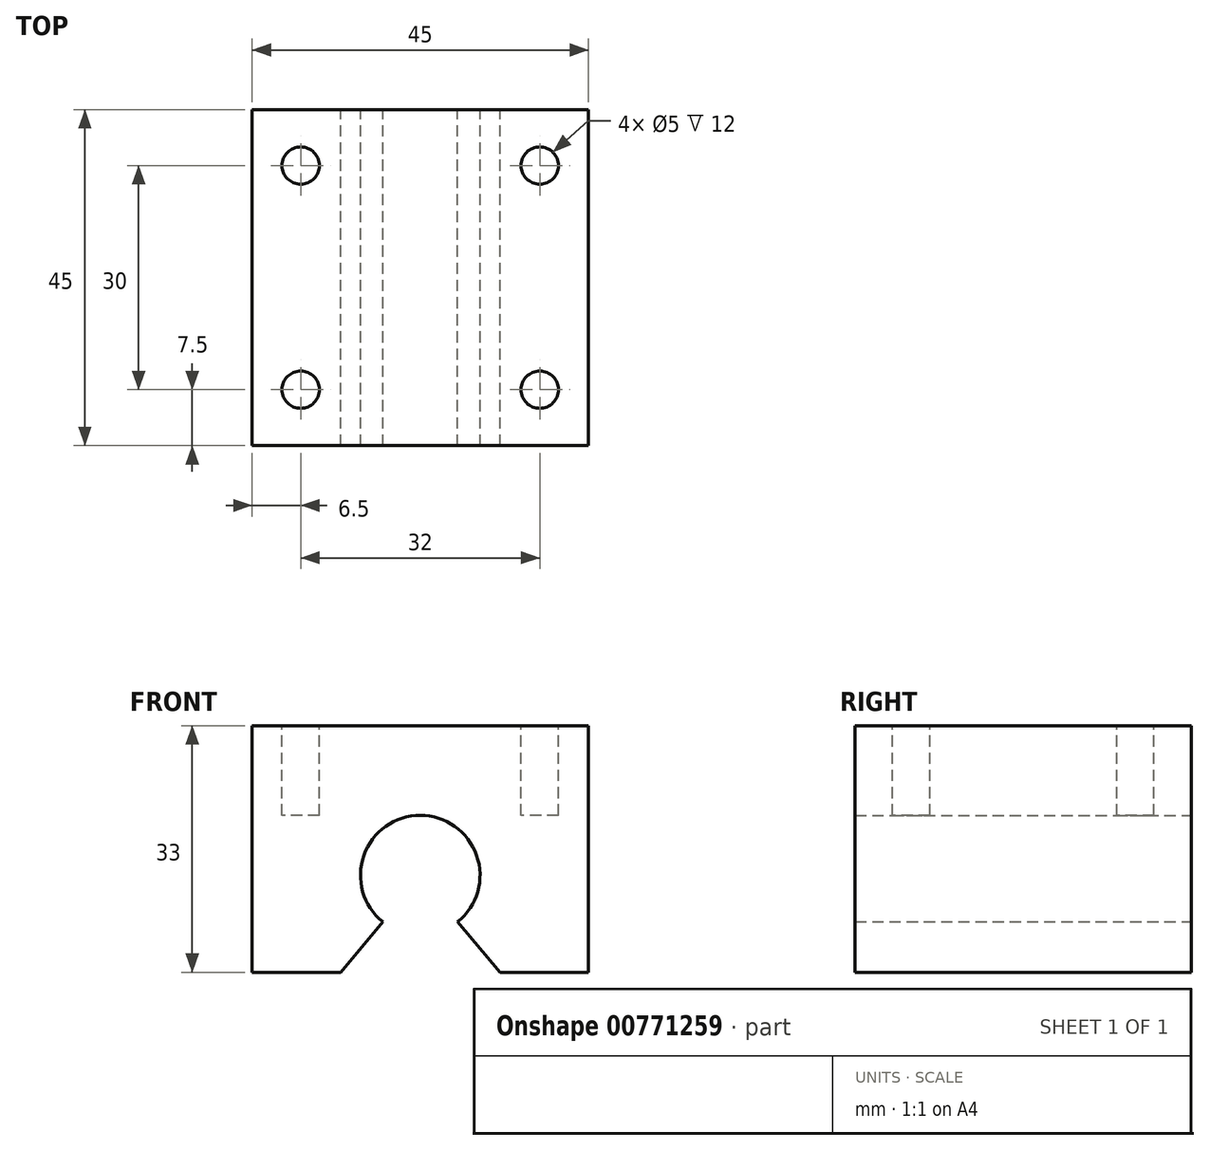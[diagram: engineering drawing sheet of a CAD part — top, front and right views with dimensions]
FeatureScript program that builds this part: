
annotation { "Feature Type Name" : "Feature", "Feature Type Description" : "" }
export const myFeature = defineFeature(function(context is Context, id is Id, definition is map)
    precondition{}
    {
        {
            var Q0;
            Q0=qCreatedBy(makeId("Front.planeOp"),FACE);
            var sketch = newSketch(context, id + "F0", { "sketchPlane" : qUnion([Q0])});
            skLineSegment(sketch, "E0.right", {"start": v(-22.5, 20) * mm, "end": v(-22.5, -13) * mm});
            skPoint(sketch, "E0.middle", {"position": v(0, 0) * mm});
            skArc(sketch, "E1", {"start": v(0, 8) * mm, "mid": v(-7.55, 2.65) * mm, "end": v(-5, -6.24) * mm});
            skLineSegment(sketch, "E2", {"start": v(-5, -6.24) * mm, "end": v(-10.67, -13) * mm});
            skLineSegment(sketch, "E3.trimOffspring", {"start": v(-10.67, -13) * mm, "end": v(-22.5, -13) * mm});
            skLineSegment(sketch, "E4", {"start": v(0, 8) * mm, "end": v(0, 20) * mm});
            skLineSegment(sketch, "E5", {"start": v(0, 20) * mm, "end": v(-22.5, 20) * mm});
            skLineSegment(sketch, "E6.MirrorCS", {"start": v(22.5, 20) * mm, "end": v(22.5, -13) * mm});
            skLineSegment(sketch, "E7.MirrorCS", {"start": v(0, 20) * mm, "end": v(22.5, 20) * mm});
            skLineSegment(sketch, "E8.MirrorCS", {"start": v(5, -6.24) * mm, "end": v(10.67, -13) * mm});
            skArc(sketch, "E9.MirrorCS", {"start": v(0, 8) * mm, "mid": v(7.55, 2.65) * mm, "end": v(5, -6.24) * mm});
            skLineSegment(sketch, "E10.MirrorCS", {"start": v(10.67, -13) * mm, "end": v(22.5, -13) * mm});
            skSolve(sketch);
        }
        {
            var Q0;
            Q0 = qSketchRegion(id + "F0", true);
            extrude(context, id + "F1", {"entities" : qUnion([Q0]), "depth" : 45 * mm, "offsetDistance" : 25 * mm});
        }
        {
            var Q0;
            Q0=makeQuery(id+"F1.opExtrude","SWEPT_FACE",FACE,{"disambiguationData":[OSD([sQuery(id+"F0.wireOp",EDGE,"E5"),sQuery(id+"F0.wireOp",EDGE,"E7.MirrorCS")])]});
            var sketch = newSketch(context, id + "F2", { "sketchPlane" : qUnion([Q0])});
            skLineSegment(sketch, "E11.bottom", {"start": v(-16, -7.5) * mm, "end": v(16, -7.5) * mm, "construction": true});
            skLineSegment(sketch, "E11.top", {"start": v(-16, -37.5) * mm, "end": v(16, -37.5) * mm, "construction": true});
            skLineSegment(sketch, "E11.left", {"start": v(-16, -7.5) * mm, "end": v(-16, -37.5) * mm, "construction": true});
            skLineSegment(sketch, "E11.right", {"start": v(16, -7.5) * mm, "end": v(16, -37.5) * mm, "construction": true});
            skPoint(sketch, "E11.middle", {"position": v(0, -22.5) * mm});
            skCircle(sketch, "E12", {"center": v(-16, -7.5) * mm, "radius": 2.5 * mm});
            skCircle(sketch, "E13", {"center": v(16, -7.5) * mm, "radius": 2.5 * mm});
            skCircle(sketch, "E14", {"center": v(16, -37.5) * mm, "radius": 2.5 * mm});
            skCircle(sketch, "E15", {"center": v(-16, -37.5) * mm, "radius": 2.5 * mm});
            skLineSegment(sketch, "E16", {"start": v(22.5, 0) * mm, "end": v(-22.5, -45) * mm, "construction": true});
            skLineSegment(sketch, "E17", {"start": v(-22.5, 0) * mm, "end": v(22.5, -45) * mm, "construction": true});
            skSolve(sketch);
        }
        {
            var Q0;
            Q0 = qSketchRegion(id + "F2", true);
            extrude(context, id + "F3", {"entities" : qUnion([Q0]), "operationType" : NewBodyOperationType.REMOVE, "oppositeDirection" : true, "depth" : 12 * mm, "offsetDistance" : 25 * mm});
        }
    });
